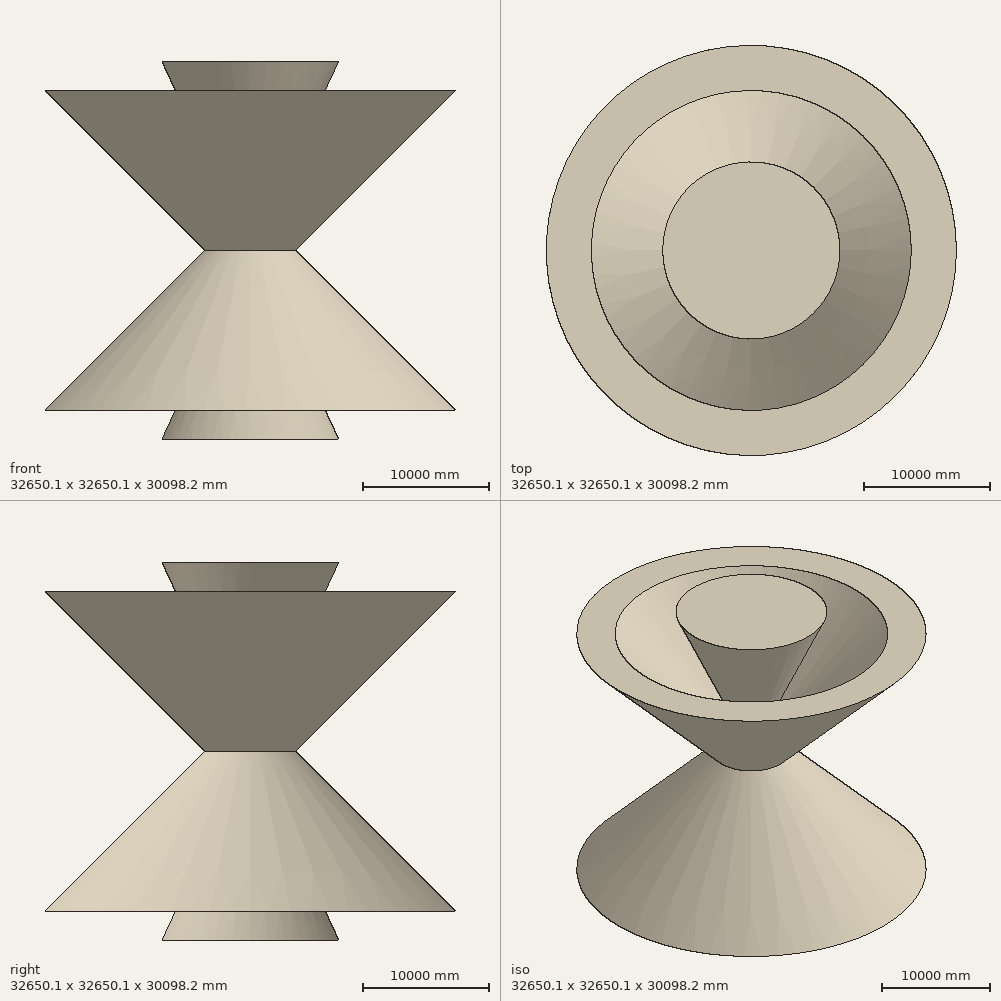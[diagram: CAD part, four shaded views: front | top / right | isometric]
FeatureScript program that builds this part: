
annotation { "Feature Type Name" : "Feature", "Feature Type Description" : "" }
export const myFeature = defineFeature(function(context is Context, id is Id, definition is map)
    precondition{}
    {
        {
            var Q0;
            Q0=qCreatedBy(makeId("Top.planeOp"),FACE);
            var sketch = newSketch(context, id + "F0", { "sketchPlane" : qUnion([Q0])});
            skCircle(sketch, "E0", {"center": v(0, 0) * mm, "radius": 32.94 * mm});
            skSolve(sketch);
        }
        {
            var Q0;
            Q0=makeQuery(id+"F0.imprint","IMPRINT",FACE,{"disambiguationData":[TD([[makeQuery(id+"F0.imprint","IMPRINT",EDGE,{"derivedFrom":sQuery(id+"F0.wireOp",EDGE,"E0")}),1.0]])]});
            extrude(context, id + "F1", {"entities" : qUnion([Q0]), "endBound" : BoundingType.SYMMETRIC, "depth" : 25400 * mm, "hasDraft" : true, "draftAngle" : 45 * degree});
        }
        {
            var Q0;
            Q0=makeQuery(id+"F1.opExtrude","CAP_FACE",FACE,{"disambiguationData":[OSD([sQuery(id+"F0.wireOp",EDGE,"E0")])],"isStart":false});
            var Q1;
            Q1=makeQuery(id+"F1.opExtrude","CAP_FACE",FACE,{"disambiguationData":[OSD([sQuery(id+"F0.wireOp",EDGE,"E0")])],"isStart":true});
            shell(context, id + "F2", {"entities" : qUnion([Q0, Q1]), "thickness" : 2540 * mm, "oppositeDirection" : true});
        }
        {
            var Q0;
            Q0=qCreatedBy(makeId("Top.planeOp"),FACE);
            var sketch = newSketch(context, id + "F3", { "sketchPlane" : qUnion([Q0])});
            skCircle(sketch, "E1", {"center": v(0, 0) * mm, "radius": 31.64 * mm});
            skSolve(sketch);
        }
        {
            var Q0;
            Q0 = qSketchRegion(id + "F3", true);
            extrude(context, id + "F4", {"entities" : qUnion([Q0]), "endBound" : BoundingType.SYMMETRIC, "depth" : 30098.2 * mm, "hasDraft" : true, "draftAngle" : 25 * degree});
        }
    });
